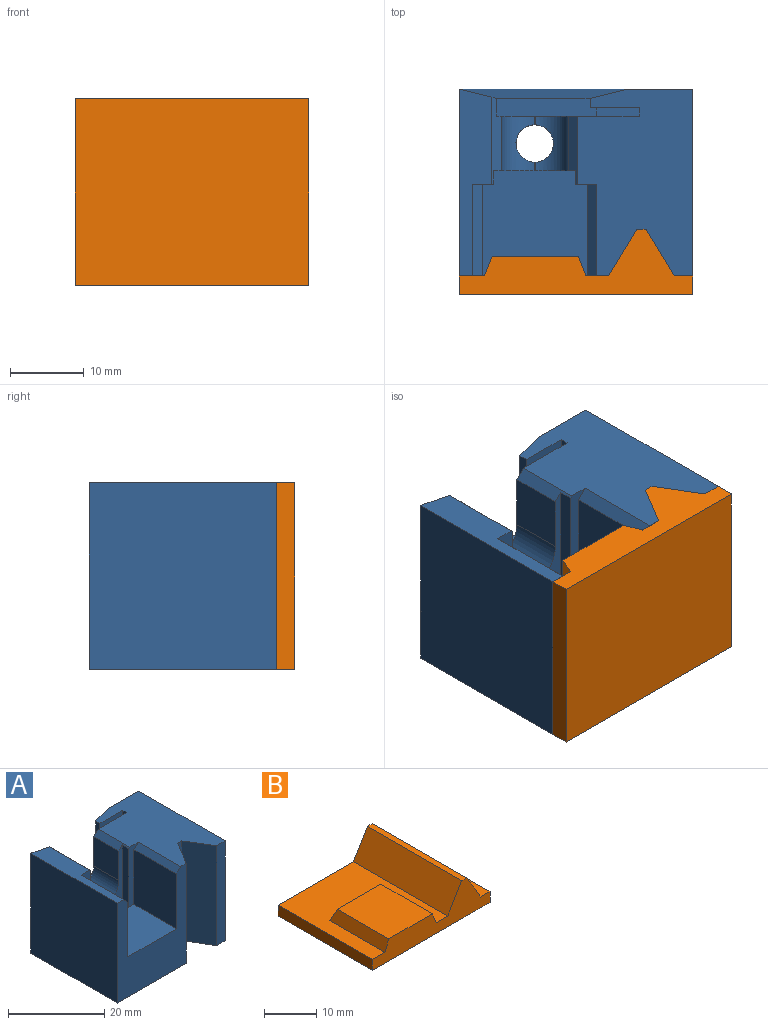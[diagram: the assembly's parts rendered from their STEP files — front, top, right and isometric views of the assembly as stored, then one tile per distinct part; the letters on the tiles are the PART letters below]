
ASSEMBLY  parts=2 mates=1
PART A: 44 faces, bbox 31.8x25.4x25.4 mm
  f0: plane 25.4x15.67mm, normal (0,0,1), area 316.6mm2, adj f1,f3,f6,f7,f9,f11,f14,f15
  f1: plane 25.4x2.54mm, normal (0,-1,0), area 64.5mm2, adj f0,f2,f11,f35
  f2: plane 31.75x25.4mm, normal (0,0,-1), area 693.1mm2, adj f1,f3,f9,f10,f11,f33,f34,f35
  f3: plane 25.4x20.32mm, normal (0,-1,0), area 297.7mm2, adj f0,f2,f10,f12,f24,f25,f29,f36
  f4: plane 1.16x0.14mm, normal (0,0,1), area 0.2mm2, adj f28,f30,f31,f32
  f5: plane 12.07x3.04mm, normal (0,1,0), area 10.2mm2, adj f8,f13,f18,f31,f43
  f6: plane 12.7x12.06mm, normal (0,1,0), area 114.1mm2, adj f0,f7,f8,f16,f17,f19,f30,f42
  f7: plane 10.92x1.14mm, normal (-1,0,0), area 12.5mm2, adj f0,f6,f14,f17
  f8: plane 13.54x2.41mm, normal (0,0,1), area 31.6mm2, adj f5,f6,f13,f14,f15,f16,f20,f38
  f9: plane 31.75x25.4mm, normal (0,1,0), area 400mm2, adj f0,f2,f10,f11,f37,f38
  f10: plane 25.4x25.4mm, normal (-1,0,0), area 645.2mm2, adj f2,f3,f9,f12,f39
  f11: plane 25.4x25.4mm, normal (1,0,0), area 645.2mm2, adj f0,f1,f2,f9
  f12: plane 25.4x4.45mm, normal (0,0,1), area 78.3mm2, adj f3,f10,f23,f39,f40,f43
  f13: plane 12.07x2.41mm, normal (1,0,0), area 29.1mm2, adj f5,f8,f39,f43
  f14: plane 12.7x6.68mm, normal (0,-1,0), area 74.5mm2, adj f0,f7,f8,f15,f16,f17
  f15: plane 12.7x1.27mm, normal (-1,0,0), area 16.1mm2, adj f0,f8,f14,f37
  f16: plane 1.78x1.14mm, normal (-1,0,0), area 2mm2, adj f6,f8,f14,f17
  f17: plane 5.84x1.14mm, normal (0,0,1), area 6.7mm2, adj f6,f7,f14,f16
  f18: plane 7.46x7.39mm, normal (1,0,0), area 55.2mm2, adj f5,f28,f31,f43
  f19: plane 7.46x7.39mm, normal (-1,0,0), area 55.2mm2, adj f6,f28,f30,f42
  f20: plane 4.28x0.51mm, normal (0,-1,0), area 1.5mm2, adj f8,f21,f30,f31
  f21: plane 1.16x0.14mm, normal (0,0,1), area 0.2mm2, adj f20,f30,f31,f32
  f22: plane 14.97x1.87mm, normal (1,0,0), area 28mm2, adj f23,f28,f29,f43
  f23: plane 15.21x2.82mm, normal (0,-1,0), area 24.4mm2, adj f12,f22,f24,f29,f40,f43
  f24: plane 13.94x12.46mm, normal (1,0,0), area 173.7mm2, adj f3,f23,f29,f40
  f25: plane 13.94x12.46mm, normal (-1,0,0), area 173.7mm2, adj f3,f26,f29,f41
  f26: plane 15.21x2.82mm, normal (0,-1,0), area 24.4mm2, adj f0,f25,f27,f29,f41,f42
  f27: plane 14.97x1.87mm, normal (-1,0,0), area 28mm2, adj f26,f28,f29,f42
  f28: plane 14.97x11.15mm, normal (0,-1,0), area 56.6mm2, adj f4,f18,f19,f22,f27,f29,f30,f31
  f29: plane 14.33x14.25mm, normal (0,0,1), area 198.3mm2, adj f3,f22,f23,f24,f25,f26,f27,f28
  f30: cylinder r=4.48mm len=7.39mm, axis (0,1,0), area 41.8mm2, adj f4,f6,f19,f20,f21,f28,f32
  f31: cylinder r=4.48mm len=7.39mm, axis (0,-1,0), area 41.8mm2, adj f4,f5,f18,f20,f21,f28,f32
  f32: cylinder r=2.54mm len=10.4mm, axis (0,0,1), area 159.7mm2, adj f4,f21,f30,f31,f33
  f33: cone r=5.08mm half-angle=45deg, axis (0,0,-1), area 86mm2, adj f2,f32
  f34: plane 25.4x1.27mm, normal (0,-1,0), area 32.3mm2, adj f0,f2,f35,f36
  f35: plane 25.4x6.35mm, normal (-0.86,-0.51,0), area 188.1mm2, adj f0,f1,f2,f34
  f36: plane 25.4x6.35mm, normal (0.86,-0.51,0), area 188.1mm2, adj f0,f2,f3,f34
  f37: plane 17.78x5.08mm, normal (-0.24,0.97,0), area 79.8mm2, adj f0,f9,f15,f38
  f38: plane 22.86x5.08mm, normal (0,0.97,0.24), area 93.1mm2, adj f8,f9,f37,f39
  f39: plane 17.78x5.08mm, normal (0.24,0.97,0), area 79.6mm2, adj f10,f12,f13,f38,f43
  f40: plane 12.46x1.27mm, normal (0.71,0,0.71), area 22.4mm2, adj f3,f12,f23,f24
  f41: plane 12.46x1.27mm, normal (-0.71,0,0.71), area 22.4mm2, adj f0,f3,f25,f26
  f42: plane 9.26x1.27mm, normal (-0.71,0,0.71), area 13.9mm2, adj f0,f6,f19,f26,f27,f28
  f43: plane 11.83x1.27mm, normal (0.71,0,0.71), area 16.2mm2, adj f5,f12,f13,f18,f22,f23,f28,f39
PART B: 14 faces, bbox 31.8x25.4x8.9 mm
  f0: plane 25.4x2.54mm, normal (0,0,1), area 64.5mm2, adj f3,f4,f5,f12
  f1: plane 25.4x20.32mm, normal (0,0,1), area 311.1mm2, adj f2,f3,f5,f8,f9,f10,f13
  f2: plane 25.4x2.54mm, normal (-1,0,0), area 64.5mm2, adj f1,f3,f5,f6
  f3: plane 31.75x8.89mm, normal (0,-1,0), area 145.9mm2, adj f0,f1,f2,f4,f6,f7,f8,f9
  f4: plane 25.4x2.54mm, normal (1,0,0), area 64.5mm2, adj f0,f3,f5,f6
  f5: plane 31.75x8.89mm, normal (0,1,0), area 112.9mm2, adj f0,f1,f2,f4,f6,f11,f12,f13
  f6: plane 31.75x25.4mm, normal (0,0,-1), area 806.5mm2, adj f2,f3,f4,f5
  f7: plane 13.84x11.71mm, normal (0,0,1), area 162.1mm2, adj f3,f8,f9,f10
  f8: plane 14.88x2.59mm, normal (-0.93,0,0.37), area 40.1mm2, adj f1,f3,f7,f10
  f9: plane 14.88x2.59mm, normal (0.93,0,0.37), area 40.1mm2, adj f1,f3,f7,f10
  f10: plane 13.78x2.59mm, normal (0,0.93,0.37), area 35.6mm2, adj f1,f7,f8,f9
  f11: plane 25.4x1.27mm, normal (0,0,1), area 32.3mm2, adj f3,f5,f12,f13
  f12: plane 25.4x6.35mm, normal (0.86,0,0.51), area 188.1mm2, adj f0,f3,f5,f11
  f13: plane 25.4x6.35mm, normal (-0.86,0,0.51), area 188.1mm2, adj f1,f3,f5,f11
PLACE A at identity
PLACE B rot(axis=(-1,0,0),90deg) t=(-41.27,-2.54,25.4)mm
MATE planar B.f3 <-> A.f0  axis (0,0,1) through (-10.58,6.35,25.4)mm
